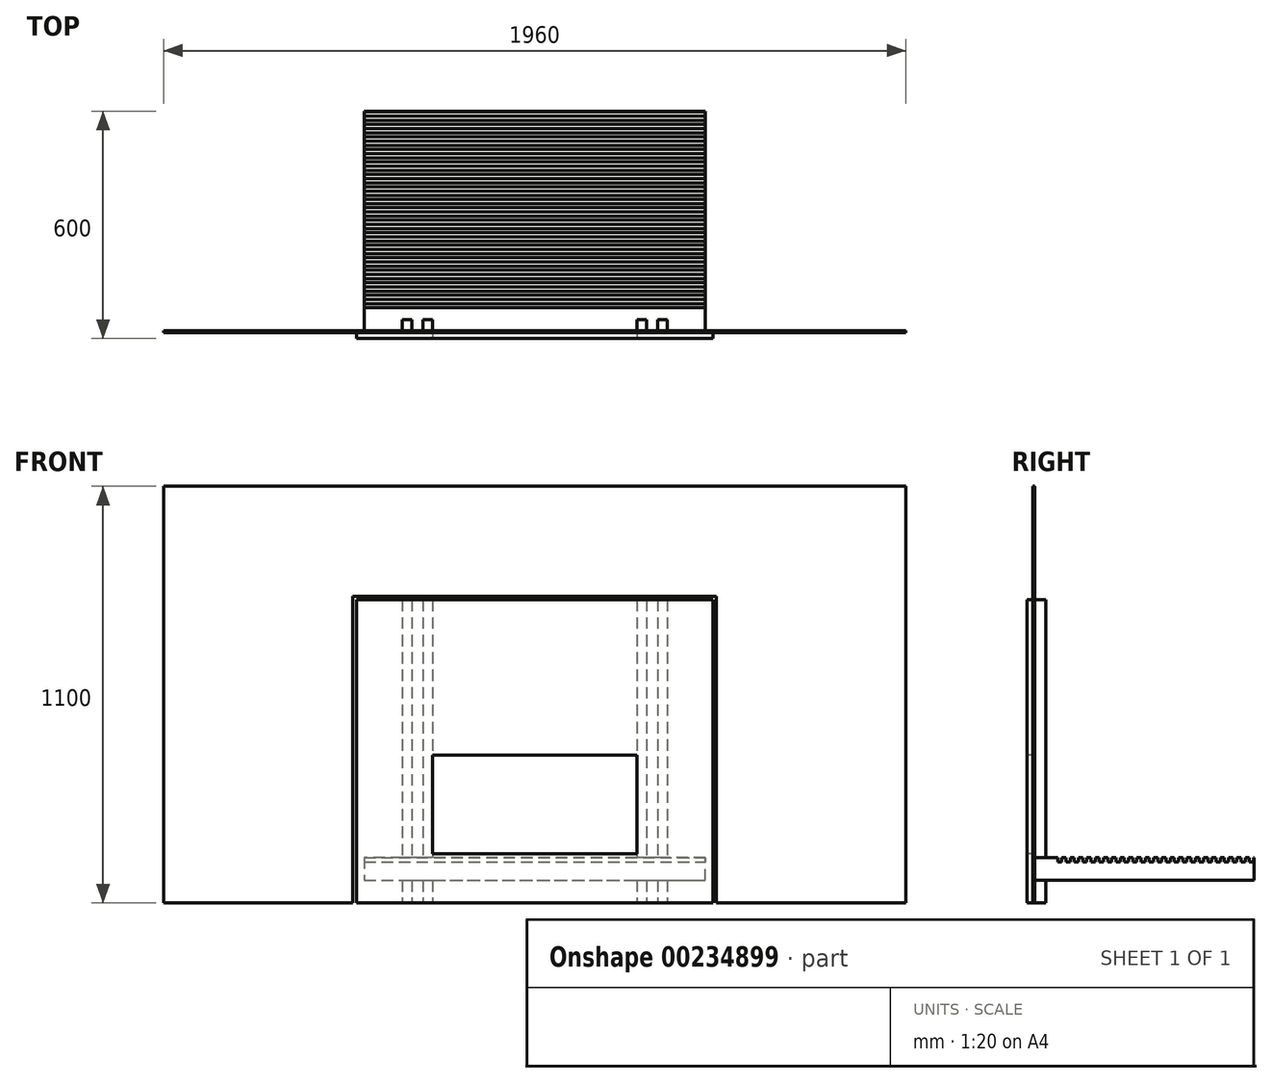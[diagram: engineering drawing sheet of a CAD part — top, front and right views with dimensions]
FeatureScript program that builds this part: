
annotation { "Feature Type Name" : "Feature", "Feature Type Description" : "" }
export const myFeature = defineFeature(function(context is Context, id is Id, definition is map)
    precondition{}
    {
        {
            var Q0;
            Q0=qCreatedBy(makeId("Front.planeOp"),FACE);
            var sketch = newSketch(context, id + "F0", { "sketchPlane" : qUnion([Q0])});
            skLineSegment(sketch, "E0.bottom", {"start": v(-270, 260) * mm, "end": v(270, 260) * mm});
            skLineSegment(sketch, "E0.top", {"start": v(-270, 0) * mm, "end": v(270, 0) * mm});
            skLineSegment(sketch, "E0.left", {"start": v(-270, 260) * mm, "end": v(-270, 0) * mm});
            skLineSegment(sketch, "E0.right", {"start": v(270, 260) * mm, "end": v(270, 0) * mm});
            skLineSegment(sketch, "E1.bottom", {"start": v(-470, 670) * mm, "end": v(470, 670) * mm});
            skLineSegment(sketch, "E1.top", {"start": v(-470, -130) * mm, "end": v(470, -130) * mm});
            skLineSegment(sketch, "E1.left", {"start": v(-470, 670) * mm, "end": v(-470, -130) * mm});
            skLineSegment(sketch, "E1.right", {"start": v(470, 670) * mm, "end": v(470, -130) * mm});
            skSolve(sketch);
        }
        {
            var Q0;
            Q0=makeQuery(id+"F0.imprint","IMPRINT",FACE,{"disambiguationData":[TD([[makeQuery(id+"F0.imprint","IMPRINT",EDGE,{"derivedFrom":sQuery(id+"F0.wireOp",EDGE,"E0.bottom")}),1.0]])]});
            extrude(context, id + "F1", {"entities" : qUnion([Q0]), "oppositeDirection" : true, "depth" : 20 * mm});
        }
        {
            var Q0;
            Q0=makeQuery(id+"F0.imprint","IMPRINT",FACE,{"disambiguationData":[TD([[makeQuery(id+"F0.imprint","IMPRINT",EDGE,{"derivedFrom":sQuery(id+"F0.wireOp",EDGE,"E0.bottom")}),-1.0]])]});
            extrude(context, id + "F2", {"entities" : qUnion([Q0]), "operationType" : NewBodyOperationType.REMOVE, "oppositeDirection" : true, "depth" : 50 * mm});
        }
        {
            var Q0;
            Q0=qCreatedBy(makeId("Front.planeOp"),FACE);
            var sketch = newSketch(context, id + "F3", { "sketchPlane" : qUnion([Q0])});
            skLineSegment(sketch, "E2.bottom", {"start": v(450, -10) * mm, "end": v(-450, -10) * mm});
            skLineSegment(sketch, "E2.top", {"start": v(-450, -70) * mm, "end": v(450, -70) * mm});
            skLineSegment(sketch, "E2.left", {"start": v(-450, -10) * mm, "end": v(-450, -70) * mm});
            skLineSegment(sketch, "E2.right", {"start": v(450, -70) * mm, "end": v(450, -10) * mm});
            skLineSegment(sketch, "E3.bottom", {"start": v(-450, -70) * mm, "end": v(-350, -70) * mm});
            skLineSegment(sketch, "E3.top", {"start": v(-450, -130) * mm, "end": v(-350, -130) * mm});
            skLineSegment(sketch, "E3.left", {"start": v(-450, -70) * mm, "end": v(-450, -130) * mm});
            skLineSegment(sketch, "E3.right", {"start": v(-350, -70) * mm, "end": v(-350, -130) * mm});
            skLineSegment(sketch, "E4.bottom", {"start": v(450, -70) * mm, "end": v(350, -70) * mm});
            skLineSegment(sketch, "E4.top", {"start": v(450, -130) * mm, "end": v(350, -130) * mm});
            skLineSegment(sketch, "E4.left", {"start": v(450, -70) * mm, "end": v(450, -130) * mm});
            skLineSegment(sketch, "E4.right", {"start": v(350, -70) * mm, "end": v(350, -130) * mm});
            skSolve(sketch);
        }
        {
            var Q0;
            Q0=makeQuery(id+"F3.imprint","IMPRINT",FACE,{"disambiguationData":[TD([[makeQuery(id+"F3.imprint","IMPRINT",EDGE,{"derivedFrom":sQuery(id+"F3.wireOp",EDGE,"E2.bottom")}),1.0]])]});
            var Q1;
            Q1=makeQuery(id+"F3.imprint","IMPRINT",FACE,{"disambiguationData":[TD([[makeQuery(id+"F3.imprint","IMPRINT",EDGE,{"derivedFrom":sQuery(id+"F3.wireOp",EDGE,"E3.bottom")}),-1.0]])]});
            var Q2;
            Q2=makeQuery(id+"F3.imprint","IMPRINT",FACE,{"disambiguationData":[TD([[makeQuery(id+"F3.imprint","IMPRINT",EDGE,{"derivedFrom":sQuery(id+"F3.wireOp",EDGE,"E4.bottom")}),1.0]])]});
            extrude(context, id + "F4", {"entities" : qUnion([Q0, Q1, Q2]), "oppositeDirection" : true, "depth" : 600 * mm});
        }
        {
            var Q0;
            Q0=makeQuery(id+"F1.opExtrude","SWEPT_BODY",BODY,{"disambiguationData":[OSD([sQuery(id+"F0.wireOp",EDGE,"E0.bottom"),sQuery(id+"F0.wireOp",EDGE,"E0.top"),sQuery(id+"F0.wireOp",EDGE,"E0.left"),sQuery(id+"F0.wireOp",EDGE,"E0.right"),sQuery(id+"F0.wireOp",EDGE,"E1.bottom"),sQuery(id+"F0.wireOp",EDGE,"E1.top"),sQuery(id+"F0.wireOp",EDGE,"E1.left"),sQuery(id+"F0.wireOp",EDGE,"E1.right")])]});
            transform(context, id + "F5", {"entities" : qUnion([Q0]), "transformType" : TransformType.TRANSLATION_3D, "dx" : 0 * mm, "dy" : -20 * mm, "dz" : 0 * mm, "makeCopy" : true});
        }
        {
            var Q0;
            Q0=makeQuery(id+"F1.opExtrude","CAP_FACE",FACE,{"disambiguationData":[OSD([sQuery(id+"F0.wireOp",EDGE,"E0.bottom"),sQuery(id+"F0.wireOp",EDGE,"E0.top"),sQuery(id+"F0.wireOp",EDGE,"E0.left"),sQuery(id+"F0.wireOp",EDGE,"E0.right"),sQuery(id+"F0.wireOp",EDGE,"E1.bottom"),sQuery(id+"F0.wireOp",EDGE,"E1.top"),sQuery(id+"F0.wireOp",EDGE,"E1.left"),sQuery(id+"F0.wireOp",EDGE,"E1.right")])],"isStart":false});
            var sketch = newSketch(context, id + "F6", { "sketchPlane" : qUnion([Q0])});
            skLineSegment(sketch, "E5.bottom", {"start": v(-350, 670) * mm, "end": v(-325, 670) * mm});
            skLineSegment(sketch, "E5.top", {"start": v(-350, -130) * mm, "end": v(-325, -130) * mm});
            skLineSegment(sketch, "E5.left", {"start": v(-350, 670) * mm, "end": v(-350, -130) * mm});
            skLineSegment(sketch, "E5.right", {"start": v(-325, 670) * mm, "end": v(-325, -130) * mm});
            skLineSegment(sketch, "E6.bottom", {"start": v(-295, 670) * mm, "end": v(-270, 670) * mm});
            skLineSegment(sketch, "E6.top", {"start": v(-295, -130) * mm, "end": v(-270, -130) * mm});
            skLineSegment(sketch, "E6.left", {"start": v(-295, 670) * mm, "end": v(-295, -130) * mm});
            skLineSegment(sketch, "E6.right", {"start": v(-270, 670) * mm, "end": v(-270, -130) * mm});
            skSolve(sketch);
        }
        {
            var Q0;
            Q0=makeQuery(id+"F6.imprint","IMPRINT",FACE,{"disambiguationData":[TD([[makeQuery(id+"F6.imprint","IMPRINT",EDGE,{"derivedFrom":sQuery(id+"F6.wireOp",EDGE,"E5.bottom")}),1.0]])]});
            var Q1;
            {var subQ2=sQuery(id+"F6.wireOp",EDGE,"E6.bottom");Q1=makeQuery(id+"F6.imprint","IMPRINT",FACE,{"disambiguationData":[TD([[makeQuery(id+"F6.imprint","IMPRINT",EDGE,{"derivedFrom":subQ2}),1.0]])]});}
            extrude(context, id + "F7", {"entities" : qUnion([Q0, Q1]), "depth" : 30 * mm});
        }
        {
            var Q0;
            Q0=makeQuery(id+"F7.opExtrude","SWEPT_BODY",BODY,{"disambiguationData":[OSD([sQuery(id+"F6.wireOp",EDGE,"E6.bottom"),sQuery(id+"F6.wireOp",EDGE,"E6.top"),sQuery(id+"F6.wireOp",EDGE,"E6.left"),sQuery(id+"F6.wireOp",EDGE,"E6.right")])]});
            var Q1;
            Q1=makeQuery(id+"F7.opExtrude","SWEPT_BODY",BODY,{"disambiguationData":[OSD([sQuery(id+"F6.wireOp",EDGE,"E5.bottom"),sQuery(id+"F6.wireOp",EDGE,"E5.top"),sQuery(id+"F6.wireOp",EDGE,"E5.left"),sQuery(id+"F6.wireOp",EDGE,"E5.right")])]});
            var Q2;
            Q2=qCreatedBy(makeId("Right.planeOp"),FACE);
            mirror(context, id + "F8", {"operationType" : NewBodyOperationType.ADD, "entities" : qUnion([Q0, Q1]), "mirrorPlane" : qUnion([Q2])});
        }
        {
            var Q0;
            Q0=makeQuery(id+"F1.opExtrude","SWEPT_BODY",BODY,{"disambiguationData":[OSD([sQuery(id+"F0.wireOp",EDGE,"E0.bottom"),sQuery(id+"F0.wireOp",EDGE,"E0.top"),sQuery(id+"F0.wireOp",EDGE,"E0.left"),sQuery(id+"F0.wireOp",EDGE,"E0.right"),sQuery(id+"F0.wireOp",EDGE,"E1.bottom"),sQuery(id+"F0.wireOp",EDGE,"E1.top"),sQuery(id+"F0.wireOp",EDGE,"E1.left"),sQuery(id+"F0.wireOp",EDGE,"E1.right")])]});
            transform(context, id + "F9", {"entities" : qUnion([Q0]), "transformType" : TransformType.TRANSLATION_3D, "dx" : 0 * mm, "dy" : -20 * mm, "dz" : 0 * mm, "makeCopy" : false});
        }
        {
            var Q0;
            Q0=makeQuery(id+"F5wjGa6SZT0iqO1_2.opExtrude","SWEPT_BODY",BODY,{"disambiguationData":[OSD([sQuery(id+"F86rnJCBxE0X9vH_2.wireOp",EDGE,"lRiHVolj-1JW2-LYaO-sivt-DGUVgLXCVF1q.bottom"),sQuery(id+"F86rnJCBxE0X9vH_2.wireOp",EDGE,"lRiHVolj-1JW2-LYaO-sivt-DGUVgLXCVF1q.top"),sQuery(id+"F86rnJCBxE0X9vH_2.wireOp",EDGE,"lRiHVolj-1JW2-LYaO-sivt-DGUVgLXCVF1q.left"),sQuery(id+"F86rnJCBxE0X9vH_2.wireOp",EDGE,"lRiHVolj-1JW2-LYaO-sivt-DGUVgLXCVF1q.right")])]});
            var Q1;
            Q1=makeQuery(id+"F5wjGa6SZT0iqO1_2.opExtrude","SWEPT_BODY",BODY,{"disambiguationData":[OSD([sQuery(id+"F86rnJCBxE0X9vH_2.wireOp",EDGE,"VoNIm3P5-RSFV-UMTa-le7R-OVk3DMM1O943.bottom"),sQuery(id+"F86rnJCBxE0X9vH_2.wireOp",EDGE,"VoNIm3P5-RSFV-UMTa-le7R-OVk3DMM1O943.top"),sQuery(id+"F86rnJCBxE0X9vH_2.wireOp",EDGE,"VoNIm3P5-RSFV-UMTa-le7R-OVk3DMM1O943.left"),sQuery(id+"F86rnJCBxE0X9vH_2.wireOp",EDGE,"VoNIm3P5-RSFV-UMTa-le7R-OVk3DMM1O943.right")])]});
            var Q2;
            Q2=makeQuery(id+"F5.opPattern","COPY",BODY,{"derivedFrom":makeQuery(id+"F1.opExtrude","SWEPT_BODY",BODY,{"disambiguationData":[OSD([sQuery(id+"F0.wireOp",EDGE,"E0.bottom"),sQuery(id+"F0.wireOp",EDGE,"E0.top"),sQuery(id+"F0.wireOp",EDGE,"E0.left"),sQuery(id+"F0.wireOp",EDGE,"E0.right"),sQuery(id+"F0.wireOp",EDGE,"E1.bottom"),sQuery(id+"F0.wireOp",EDGE,"E1.top"),sQuery(id+"F0.wireOp",EDGE,"E1.left"),sQuery(id+"F0.wireOp",EDGE,"E1.right")])]}),"instanceName":"1"});
            deleteBodies(context, id + "F10", {"entities" : qUnion([Q0, Q1, Q2])});
        }
        {
            var Q0;
            Q0=makeQuery(id+"F4.opExtrude","SWEPT_FACE",FACE,{"disambiguationData":[OSD([sQuery(id+"F3.wireOp",EDGE,"E2.right"),sQuery(id+"F3.wireOp",EDGE,"E4.left")])]});
            var sketch = newSketch(context, id + "F11", { "sketchPlane" : qUnion([Q0])});
            skLineSegment(sketch, "E7.bottom", {"start": v(61, -10) * mm, "end": v(72, -10) * mm});
            skLineSegment(sketch, "E7.top", {"start": v(61, -21) * mm, "end": v(72, -21) * mm});
            skLineSegment(sketch, "E7.left", {"start": v(61, -10) * mm, "end": v(61, -21) * mm});
            skLineSegment(sketch, "E7.right", {"start": v(72, -10) * mm, "end": v(72, -21) * mm});
            skLineSegment(sketch, "E8.1.0.0", {"start": v(94, -10) * mm, "end": v(94, -21) * mm});
            skLineSegment(sketch, "E8.1.0.1", {"start": v(83, -10) * mm, "end": v(83, -21) * mm});
            skLineSegment(sketch, "E8.1.0.2", {"start": v(83, -21) * mm, "end": v(94, -21) * mm});
            skLineSegment(sketch, "E8.1.0.3", {"start": v(83, -10) * mm, "end": v(94, -10) * mm});
            skLineSegment(sketch, "E8.2.0.0", {"start": v(116, -10) * mm, "end": v(116, -21) * mm});
            skLineSegment(sketch, "E8.2.0.1", {"start": v(105, -10) * mm, "end": v(105, -21) * mm});
            skLineSegment(sketch, "E8.2.0.2", {"start": v(105, -21) * mm, "end": v(116, -21) * mm});
            skLineSegment(sketch, "E8.2.0.3", {"start": v(105, -10) * mm, "end": v(116, -10) * mm});
            skLineSegment(sketch, "E8.3.0.0", {"start": v(138, -10) * mm, "end": v(138, -21) * mm});
            skLineSegment(sketch, "E8.3.0.1", {"start": v(127, -10) * mm, "end": v(127, -21) * mm});
            skLineSegment(sketch, "E8.3.0.2", {"start": v(127, -21) * mm, "end": v(138, -21) * mm});
            skLineSegment(sketch, "E8.3.0.3", {"start": v(127, -10) * mm, "end": v(138, -10) * mm});
            skLineSegment(sketch, "E8.4.0.0", {"start": v(160, -10) * mm, "end": v(160, -21) * mm});
            skLineSegment(sketch, "E8.4.0.1", {"start": v(149, -10) * mm, "end": v(149, -21) * mm});
            skLineSegment(sketch, "E8.4.0.2", {"start": v(149, -21) * mm, "end": v(160, -21) * mm});
            skLineSegment(sketch, "E8.4.0.3", {"start": v(149, -10) * mm, "end": v(160, -10) * mm});
            skLineSegment(sketch, "E8.5.0.0", {"start": v(182, -10) * mm, "end": v(182, -21) * mm});
            skLineSegment(sketch, "E8.5.0.1", {"start": v(171, -10) * mm, "end": v(171, -21) * mm});
            skLineSegment(sketch, "E8.5.0.2", {"start": v(171, -21) * mm, "end": v(182, -21) * mm});
            skLineSegment(sketch, "E8.5.0.3", {"start": v(171, -10) * mm, "end": v(182, -10) * mm});
            skLineSegment(sketch, "E8.6.0.0", {"start": v(204, -10) * mm, "end": v(204, -21) * mm});
            skLineSegment(sketch, "E8.6.0.1", {"start": v(193, -10) * mm, "end": v(193, -21) * mm});
            skLineSegment(sketch, "E8.6.0.2", {"start": v(193, -21) * mm, "end": v(204, -21) * mm});
            skLineSegment(sketch, "E8.6.0.3", {"start": v(193, -10) * mm, "end": v(204, -10) * mm});
            skLineSegment(sketch, "E8.7.0.0", {"start": v(226, -10) * mm, "end": v(226, -21) * mm});
            skLineSegment(sketch, "E8.7.0.1", {"start": v(215, -10) * mm, "end": v(215, -21) * mm});
            skLineSegment(sketch, "E8.7.0.2", {"start": v(215, -21) * mm, "end": v(226, -21) * mm});
            skLineSegment(sketch, "E8.7.0.3", {"start": v(215, -10) * mm, "end": v(226, -10) * mm});
            skLineSegment(sketch, "E8.8.0.0", {"start": v(248, -10) * mm, "end": v(248, -21) * mm});
            skLineSegment(sketch, "E8.8.0.1", {"start": v(237, -10) * mm, "end": v(237, -21) * mm});
            skLineSegment(sketch, "E8.8.0.2", {"start": v(237, -21) * mm, "end": v(248, -21) * mm});
            skLineSegment(sketch, "E8.8.0.3", {"start": v(237, -10) * mm, "end": v(248, -10) * mm});
            skLineSegment(sketch, "E8.9.0.0", {"start": v(270, -10) * mm, "end": v(270, -21) * mm});
            skLineSegment(sketch, "E8.9.0.1", {"start": v(259, -10) * mm, "end": v(259, -21) * mm});
            skLineSegment(sketch, "E8.9.0.2", {"start": v(259, -21) * mm, "end": v(270, -21) * mm});
            skLineSegment(sketch, "E8.9.0.3", {"start": v(259, -10) * mm, "end": v(270, -10) * mm});
            skLineSegment(sketch, "E8.10.0.0", {"start": v(292, -10) * mm, "end": v(292, -21) * mm});
            skLineSegment(sketch, "E8.10.0.1", {"start": v(281, -10) * mm, "end": v(281, -21) * mm});
            skLineSegment(sketch, "E8.10.0.2", {"start": v(281, -21) * mm, "end": v(292, -21) * mm});
            skLineSegment(sketch, "E8.10.0.3", {"start": v(281, -10) * mm, "end": v(292, -10) * mm});
            skLineSegment(sketch, "E8.11.0.0", {"start": v(314, -10) * mm, "end": v(314, -21) * mm});
            skLineSegment(sketch, "E8.11.0.1", {"start": v(303, -10) * mm, "end": v(303, -21) * mm});
            skLineSegment(sketch, "E8.11.0.2", {"start": v(303, -21) * mm, "end": v(314, -21) * mm});
            skLineSegment(sketch, "E8.11.0.3", {"start": v(303, -10) * mm, "end": v(314, -10) * mm});
            skLineSegment(sketch, "E8.12.0.0", {"start": v(336, -10) * mm, "end": v(336, -21) * mm});
            skLineSegment(sketch, "E8.12.0.1", {"start": v(325, -10) * mm, "end": v(325, -21) * mm});
            skLineSegment(sketch, "E8.12.0.2", {"start": v(325, -21) * mm, "end": v(336, -21) * mm});
            skLineSegment(sketch, "E8.12.0.3", {"start": v(325, -10) * mm, "end": v(336, -10) * mm});
            skLineSegment(sketch, "E8.13.0.0", {"start": v(358, -10) * mm, "end": v(358, -21) * mm});
            skLineSegment(sketch, "E8.13.0.1", {"start": v(347, -10) * mm, "end": v(347, -21) * mm});
            skLineSegment(sketch, "E8.13.0.2", {"start": v(347, -21) * mm, "end": v(358, -21) * mm});
            skLineSegment(sketch, "E8.13.0.3", {"start": v(347, -10) * mm, "end": v(358, -10) * mm});
            skLineSegment(sketch, "E8.14.0.0", {"start": v(380, -10) * mm, "end": v(380, -21) * mm});
            skLineSegment(sketch, "E8.14.0.1", {"start": v(369, -10) * mm, "end": v(369, -21) * mm});
            skLineSegment(sketch, "E8.14.0.2", {"start": v(369, -21) * mm, "end": v(380, -21) * mm});
            skLineSegment(sketch, "E8.14.0.3", {"start": v(369, -10) * mm, "end": v(380, -10) * mm});
            skLineSegment(sketch, "E8.15.0.0", {"start": v(402, -10) * mm, "end": v(402, -21) * mm});
            skLineSegment(sketch, "E8.15.0.1", {"start": v(391, -10) * mm, "end": v(391, -21) * mm});
            skLineSegment(sketch, "E8.15.0.2", {"start": v(391, -21) * mm, "end": v(402, -21) * mm});
            skLineSegment(sketch, "E8.15.0.3", {"start": v(391, -10) * mm, "end": v(402, -10) * mm});
            skLineSegment(sketch, "E8.16.0.0", {"start": v(424, -10) * mm, "end": v(424, -21) * mm});
            skLineSegment(sketch, "E8.16.0.1", {"start": v(413, -10) * mm, "end": v(413, -21) * mm});
            skLineSegment(sketch, "E8.16.0.2", {"start": v(413, -21) * mm, "end": v(424, -21) * mm});
            skLineSegment(sketch, "E8.16.0.3", {"start": v(413, -10) * mm, "end": v(424, -10) * mm});
            skLineSegment(sketch, "E8.17.0.0", {"start": v(446, -10) * mm, "end": v(446, -21) * mm});
            skLineSegment(sketch, "E8.17.0.1", {"start": v(435, -10) * mm, "end": v(435, -21) * mm});
            skLineSegment(sketch, "E8.17.0.2", {"start": v(435, -21) * mm, "end": v(446, -21) * mm});
            skLineSegment(sketch, "E8.17.0.3", {"start": v(435, -10) * mm, "end": v(446, -10) * mm});
            skLineSegment(sketch, "E8.18.0.0", {"start": v(468, -10) * mm, "end": v(468, -21) * mm});
            skLineSegment(sketch, "E8.18.0.1", {"start": v(457, -10) * mm, "end": v(457, -21) * mm});
            skLineSegment(sketch, "E8.18.0.2", {"start": v(457, -21) * mm, "end": v(468, -21) * mm});
            skLineSegment(sketch, "E8.18.0.3", {"start": v(457, -10) * mm, "end": v(468, -10) * mm});
            skLineSegment(sketch, "E8.19.0.0", {"start": v(490, -10) * mm, "end": v(490, -21) * mm});
            skLineSegment(sketch, "E8.19.0.1", {"start": v(479, -10) * mm, "end": v(479, -21) * mm});
            skLineSegment(sketch, "E8.19.0.2", {"start": v(479, -21) * mm, "end": v(490, -21) * mm});
            skLineSegment(sketch, "E8.19.0.3", {"start": v(479, -10) * mm, "end": v(490, -10) * mm});
            skLineSegment(sketch, "E8.20.0.0", {"start": v(512, -10) * mm, "end": v(512, -21) * mm});
            skLineSegment(sketch, "E8.20.0.1", {"start": v(501, -10) * mm, "end": v(501, -21) * mm});
            skLineSegment(sketch, "E8.20.0.2", {"start": v(501, -21) * mm, "end": v(512, -21) * mm});
            skLineSegment(sketch, "E8.20.0.3", {"start": v(501, -10) * mm, "end": v(512, -10) * mm});
            skLineSegment(sketch, "E8.21.0.0", {"start": v(534, -10) * mm, "end": v(534, -21) * mm});
            skLineSegment(sketch, "E8.21.0.1", {"start": v(523, -10) * mm, "end": v(523, -21) * mm});
            skLineSegment(sketch, "E8.21.0.2", {"start": v(523, -21) * mm, "end": v(534, -21) * mm});
            skLineSegment(sketch, "E8.21.0.3", {"start": v(523, -10) * mm, "end": v(534, -10) * mm});
            skLineSegment(sketch, "E8.22.0.0", {"start": v(556, -10) * mm, "end": v(556, -21) * mm});
            skLineSegment(sketch, "E8.22.0.1", {"start": v(545, -10) * mm, "end": v(545, -21) * mm});
            skLineSegment(sketch, "E8.22.0.2", {"start": v(545, -21) * mm, "end": v(556, -21) * mm});
            skLineSegment(sketch, "E8.22.0.3", {"start": v(545, -10) * mm, "end": v(556, -10) * mm});
            skLineSegment(sketch, "E8.23.0.0", {"start": v(578, -10) * mm, "end": v(578, -21) * mm});
            skLineSegment(sketch, "E8.23.0.1", {"start": v(567, -10) * mm, "end": v(567, -21) * mm});
            skLineSegment(sketch, "E8.23.0.2", {"start": v(567, -21) * mm, "end": v(578, -21) * mm});
            skLineSegment(sketch, "E8.23.0.3", {"start": v(567, -10) * mm, "end": v(578, -10) * mm});
            skLineSegment(sketch, "E8.direction1", {"start": v(61, -21) * mm, "end": v(83, -21) * mm, "construction": true});
            skSolve(sketch);
        }
        {
            var Q0;
            Q0=makeQuery(id+"F11.imprint","IMPRINT",FACE,{"disambiguationData":[TD([[makeQuery(id+"F11.imprint","IMPRINT",EDGE,{"derivedFrom":sQuery(id+"F11.wireOp",EDGE,"E7.bottom")}),1.0]])]});
            var Q1;
            Q1=makeQuery(id+"F11.imprint","IMPRINT",FACE,{"disambiguationData":[TD([[makeQuery(id+"F11.imprint","IMPRINT",EDGE,{"derivedFrom":sQuery(id+"F11.wireOp",EDGE,"E8.1.0.0")}),-1.0]])]});
            var Q2;
            Q2=makeQuery(id+"F11.imprint","IMPRINT",FACE,{"disambiguationData":[TD([[makeQuery(id+"F11.imprint","IMPRINT",EDGE,{"derivedFrom":sQuery(id+"F11.wireOp",EDGE,"E8.2.0.0")}),-1.0]])]});
            var Q3;
            Q3=makeQuery(id+"F11.imprint","IMPRINT",FACE,{"disambiguationData":[TD([[makeQuery(id+"F11.imprint","IMPRINT",EDGE,{"derivedFrom":sQuery(id+"F11.wireOp",EDGE,"E8.3.0.0")}),-1.0]])]});
            var Q4;
            Q4=makeQuery(id+"F11.imprint","IMPRINT",FACE,{"disambiguationData":[TD([[makeQuery(id+"F11.imprint","IMPRINT",EDGE,{"derivedFrom":sQuery(id+"F11.wireOp",EDGE,"E8.4.0.0")}),-1.0]])]});
            var Q5;
            Q5=makeQuery(id+"F11.imprint","IMPRINT",FACE,{"disambiguationData":[TD([[makeQuery(id+"F11.imprint","IMPRINT",EDGE,{"derivedFrom":sQuery(id+"F11.wireOp",EDGE,"E8.5.0.0")}),-1.0]])]});
            var Q6;
            Q6=makeQuery(id+"F11.imprint","IMPRINT",FACE,{"disambiguationData":[TD([[makeQuery(id+"F11.imprint","IMPRINT",EDGE,{"derivedFrom":sQuery(id+"F11.wireOp",EDGE,"E8.6.0.0")}),-1.0]])]});
            var Q7;
            Q7=makeQuery(id+"F11.imprint","IMPRINT",FACE,{"disambiguationData":[TD([[makeQuery(id+"F11.imprint","IMPRINT",EDGE,{"derivedFrom":sQuery(id+"F11.wireOp",EDGE,"E8.7.0.0")}),-1.0]])]});
            var Q8;
            Q8=makeQuery(id+"F11.imprint","IMPRINT",FACE,{"disambiguationData":[TD([[makeQuery(id+"F11.imprint","IMPRINT",EDGE,{"derivedFrom":sQuery(id+"F11.wireOp",EDGE,"E8.8.0.0")}),-1.0]])]});
            var Q9;
            Q9=makeQuery(id+"F11.imprint","IMPRINT",FACE,{"disambiguationData":[TD([[makeQuery(id+"F11.imprint","IMPRINT",EDGE,{"derivedFrom":sQuery(id+"F11.wireOp",EDGE,"E8.9.0.0")}),-1.0]])]});
            var Q10;
            Q10=makeQuery(id+"F11.imprint","IMPRINT",FACE,{"disambiguationData":[TD([[makeQuery(id+"F11.imprint","IMPRINT",EDGE,{"derivedFrom":sQuery(id+"F11.wireOp",EDGE,"E8.10.0.0")}),-1.0]])]});
            var Q11;
            Q11=makeQuery(id+"F11.imprint","IMPRINT",FACE,{"disambiguationData":[TD([[makeQuery(id+"F11.imprint","IMPRINT",EDGE,{"derivedFrom":sQuery(id+"F11.wireOp",EDGE,"E8.11.0.0")}),-1.0]])]});
            var Q12;
            Q12=makeQuery(id+"F11.imprint","IMPRINT",FACE,{"disambiguationData":[TD([[makeQuery(id+"F11.imprint","IMPRINT",EDGE,{"derivedFrom":sQuery(id+"F11.wireOp",EDGE,"E8.12.0.0")}),-1.0]])]});
            var Q13;
            Q13=makeQuery(id+"F11.imprint","IMPRINT",FACE,{"disambiguationData":[TD([[makeQuery(id+"F11.imprint","IMPRINT",EDGE,{"derivedFrom":sQuery(id+"F11.wireOp",EDGE,"E8.13.0.0")}),-1.0]])]});
            var Q14;
            Q14=makeQuery(id+"F11.imprint","IMPRINT",FACE,{"disambiguationData":[TD([[makeQuery(id+"F11.imprint","IMPRINT",EDGE,{"derivedFrom":sQuery(id+"F11.wireOp",EDGE,"E8.14.0.0")}),-1.0]])]});
            var Q15;
            Q15=makeQuery(id+"F11.imprint","IMPRINT",FACE,{"disambiguationData":[TD([[makeQuery(id+"F11.imprint","IMPRINT",EDGE,{"derivedFrom":sQuery(id+"F11.wireOp",EDGE,"E8.15.0.0")}),-1.0]])]});
            var Q16;
            Q16=makeQuery(id+"F11.imprint","IMPRINT",FACE,{"disambiguationData":[TD([[makeQuery(id+"F11.imprint","IMPRINT",EDGE,{"derivedFrom":sQuery(id+"F11.wireOp",EDGE,"E8.16.0.0")}),-1.0]])]});
            var Q17;
            Q17=makeQuery(id+"F11.imprint","IMPRINT",FACE,{"disambiguationData":[TD([[makeQuery(id+"F11.imprint","IMPRINT",EDGE,{"derivedFrom":sQuery(id+"F11.wireOp",EDGE,"E8.17.0.0")}),-1.0]])]});
            var Q18;
            Q18=makeQuery(id+"F11.imprint","IMPRINT",FACE,{"disambiguationData":[TD([[makeQuery(id+"F11.imprint","IMPRINT",EDGE,{"derivedFrom":sQuery(id+"F11.wireOp",EDGE,"E8.18.0.0")}),-1.0]])]});
            var Q19;
            Q19=makeQuery(id+"F11.imprint","IMPRINT",FACE,{"disambiguationData":[TD([[makeQuery(id+"F11.imprint","IMPRINT",EDGE,{"derivedFrom":sQuery(id+"F11.wireOp",EDGE,"E8.19.0.0")}),-1.0]])]});
            var Q20;
            Q20=makeQuery(id+"F11.imprint","IMPRINT",FACE,{"disambiguationData":[TD([[makeQuery(id+"F11.imprint","IMPRINT",EDGE,{"derivedFrom":sQuery(id+"F11.wireOp",EDGE,"E8.20.0.0")}),-1.0]])]});
            var Q21;
            Q21=makeQuery(id+"F11.imprint","IMPRINT",FACE,{"disambiguationData":[TD([[makeQuery(id+"F11.imprint","IMPRINT",EDGE,{"derivedFrom":sQuery(id+"F11.wireOp",EDGE,"E8.21.0.0")}),-1.0]])]});
            var Q22;
            Q22=makeQuery(id+"F11.imprint","IMPRINT",FACE,{"disambiguationData":[TD([[makeQuery(id+"F11.imprint","IMPRINT",EDGE,{"derivedFrom":sQuery(id+"F11.wireOp",EDGE,"E8.22.0.0")}),-1.0]])]});
            var Q23;
            Q23=makeQuery(id+"F11.imprint","IMPRINT",FACE,{"disambiguationData":[TD([[makeQuery(id+"F11.imprint","IMPRINT",EDGE,{"derivedFrom":sQuery(id+"F11.wireOp",EDGE,"E8.23.0.0")}),-1.0]])]});
            extrude(context, id + "F12", {"entities" : qUnion([Q0, Q1, Q2, Q3, Q4, Q5, Q6, Q7, Q8, Q9, Q10, Q11, Q12, Q13, Q14, Q15, Q16, Q17, Q18, Q19, Q20, Q21, Q22, Q23]), "operationType" : NewBodyOperationType.REMOVE, "endBound" : BoundingType.UP_TO_NEXT, "oppositeDirection" : true, "depth" : 25 * mm});
        }
        {
            var Q0;
            Q0=qCreatedBy(makeId("Front.planeOp"),FACE);
            var sketch = newSketch(context, id + "F13", { "sketchPlane" : qUnion([Q0])});
            skLineSegment(sketch, "E9", {"start": v(-480, -130) * mm, "end": v(-980, -130) * mm});
            skLineSegment(sketch, "E10", {"start": v(-980, -130) * mm, "end": v(-980, 970) * mm});
            skLineSegment(sketch, "E11", {"start": v(-980, 970) * mm, "end": v(980, 970) * mm});
            skLineSegment(sketch, "E12", {"start": v(980, 970) * mm, "end": v(980, -130) * mm});
            skLineSegment(sketch, "E13", {"start": v(980, -130) * mm, "end": v(480, -130) * mm});
            skLineSegment(sketch, "E14", {"start": v(480, -130) * mm, "end": v(480, 680) * mm});
            skLineSegment(sketch, "E15", {"start": v(480, 680) * mm, "end": v(-480, 680) * mm});
            skLineSegment(sketch, "E16", {"start": v(-480, 680) * mm, "end": v(-480, -130) * mm});
            skSolve(sketch);
        }
        {
            var Q0;
            Q0=makeQuery(id+"F13.imprint","IMPRINT",FACE,{"disambiguationData":[TD([[makeQuery(id+"F13.imprint","IMPRINT",EDGE,{"derivedFrom":sQuery(id+"F13.wireOp",EDGE,"E9")}),-1.0]])]});
            extrude(context, id + "F14", {"entities" : qUnion([Q0]), "operationType" : NewBodyOperationType.ADD, "depth" : 5 * mm});
        }
    });
